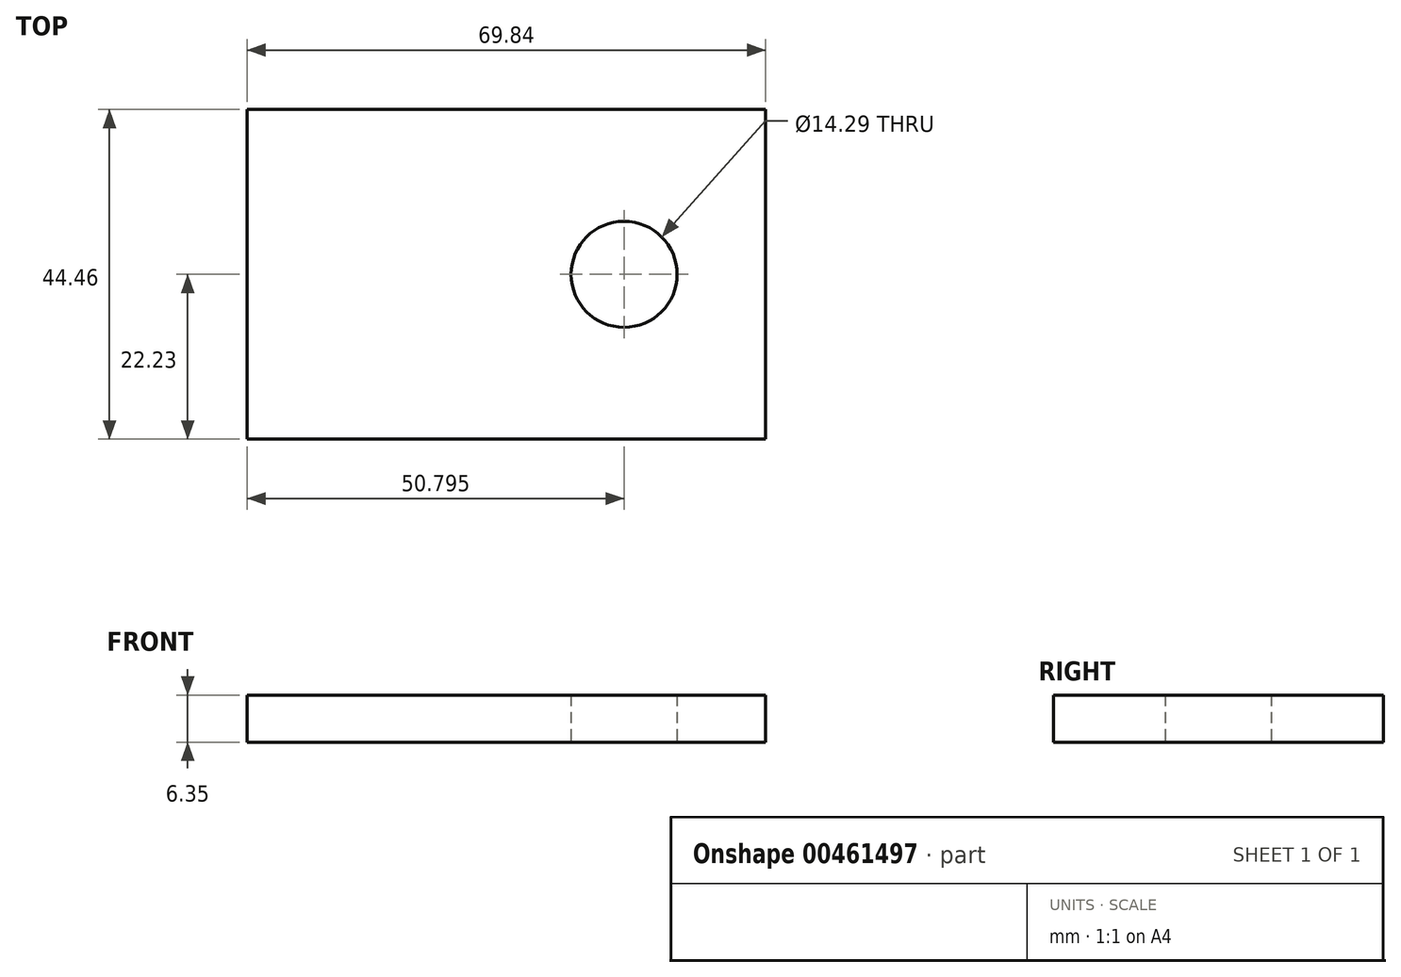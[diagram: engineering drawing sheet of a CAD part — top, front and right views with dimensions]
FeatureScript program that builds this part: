
annotation { "Feature Type Name" : "Feature", "Feature Type Description" : "" }
export const myFeature = defineFeature(function(context is Context, id is Id, definition is map)
    precondition{}
    {
        {
            var Q0;
            Q0=qCreatedBy(makeId("Top.planeOp"),FACE);
            var sketch = newSketch(context, id + "F0", { "sketchPlane" : qUnion([Q0])});
            skLineSegment(sketch, "E0.bottom", {"start": v(34.93, -22.22) * mm, "end": v(-34.93, -22.23) * mm});
            skLineSegment(sketch, "E0.top", {"start": v(34.93, 22.23) * mm, "end": v(-34.93, 22.22) * mm});
            skLineSegment(sketch, "E0.left", {"start": v(34.93, -22.22) * mm, "end": v(34.93, 22.23) * mm});
            skLineSegment(sketch, "E0.right", {"start": v(-34.93, -22.23) * mm, "end": v(-34.93, 22.22) * mm});
            skPoint(sketch, "E0.middle", {"position": v(0, 0) * mm});
            skCircle(sketch, "E1", {"center": v(15.88, 0) * mm, "radius": 7.14 * mm});
            skSolve(sketch);
        }
        {
            var Q0;
            Q0 = qSketchRegion(id + "F0", true);
            extrude(context, id + "F1", {"entities" : qUnion([Q0]), "depth" : 6.35 * mm});
        }
    });
